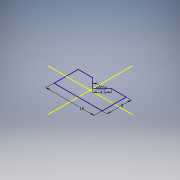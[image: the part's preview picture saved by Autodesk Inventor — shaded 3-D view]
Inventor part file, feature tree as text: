
AUTODESK INVENTOR PART (.ipt)
format: ipt  version: 2016 (Build 200138000, 138)  size: 86,016 bytes
history: native  units: mm
features: sketch x1
ambient origin geometry x8: Origin, YZ Plane, XZ Plane, XY Plane, X Axis, Y Axis, Z Axis, Center Point
feature tree (1):
  sketch  "Sketch1"  dims[d0=90.0deg d1=4.5mm d2=16.0mm d3=8.0mm]
